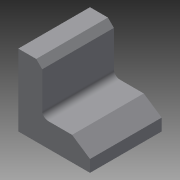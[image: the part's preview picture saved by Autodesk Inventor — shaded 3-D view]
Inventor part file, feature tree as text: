
AUTODESK INVENTOR PART (.ipt)
format: ipt  version: 2015 (Build 190159000, 159)  size: 89,600 bytes
history: native  units: in
note: dims shown in document units (in); Inventor stores cm internally (conversion verified against a paired STEP export)
features: chamfer x2, extrude x1, fillet x1, sketch x1
ambient origin geometry x8: Origin, YZ Plane, XZ Plane, XY Plane, X Axis, Y Axis, Z Axis, Center Point
bodies: Solid1 (feature_tree)
feature tree (5):
  extrude  "Extrusion1"  Depth=1.0in
  fillet  "Fillet1"  Radius=1.5in
  chamfer  "Chamfer1"  Distance=0.5in
  chamfer  "Chamfer2"  Distance=1.5in
  sketch  "Sketch1"  dims[d0=1.5in d1=1.0in d2=1.5in d3=0.5in d4=1.5in d5=0.0in d6=0.125in d9=0.125in d10=0.125in d11=45.0deg d12=0.25in d13=0.375in d14=45.0deg]
